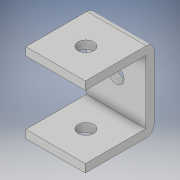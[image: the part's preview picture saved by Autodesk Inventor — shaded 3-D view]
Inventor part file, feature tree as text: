
AUTODESK INVENTOR PART (.ipt)
format: ipt  version: 2018 (Build 220112000, 112)  size: 137,728 bytes
history: native  units: in
note: dims shown in document units (in); Inventor stores cm internally (conversion verified against a paired STEP export)
features: extrude x4, sketch x4, fillet x1, projected_geometry x1
ambient origin geometry x8: Origin, YZ Plane, XZ Plane, XY Plane, X Axis, Y Axis, Z Axis, Center Point
bodies: Solid1 (feature_tree)
feature tree (10):
  extrude  "Extrusion1"  Depth=1.275in
  extrude  "Extrusion2"  TaperAngle=0.0deg  [1 undecoded]
  extrude  "Extrusion3"  Depth=0.13in
  fillet  "Fillet1"  Radius=0.13in
  extrude  "Extrusion4"  Depth=0.125in
  sketch  "Sketch1"  dims[d0=0.95in d1=1.275in]
  sketch  "Sketch2"  dims[d2=1.1in d3=0.0in d4=0.0in]
  sketch  "Sketch3"  dims[d5=0.13in d6=0.13in d7=0.13in]
  projected_geometry  "Projected Loop1"
  sketch  "Sketch4"  dims[d8=1.375in d9=0.0in d10=0.25in d11=1.375in d12=0.0in d13=0.125in d14=0.25in d15=0.475in d16=0.485in d17=1.375in d18=0.0in]
note: 1 required parameter value undecoded (feature->parameter linkage not recoverable at this tier; creation-order binding heuristic only, values carry confidence <= 0.55)
